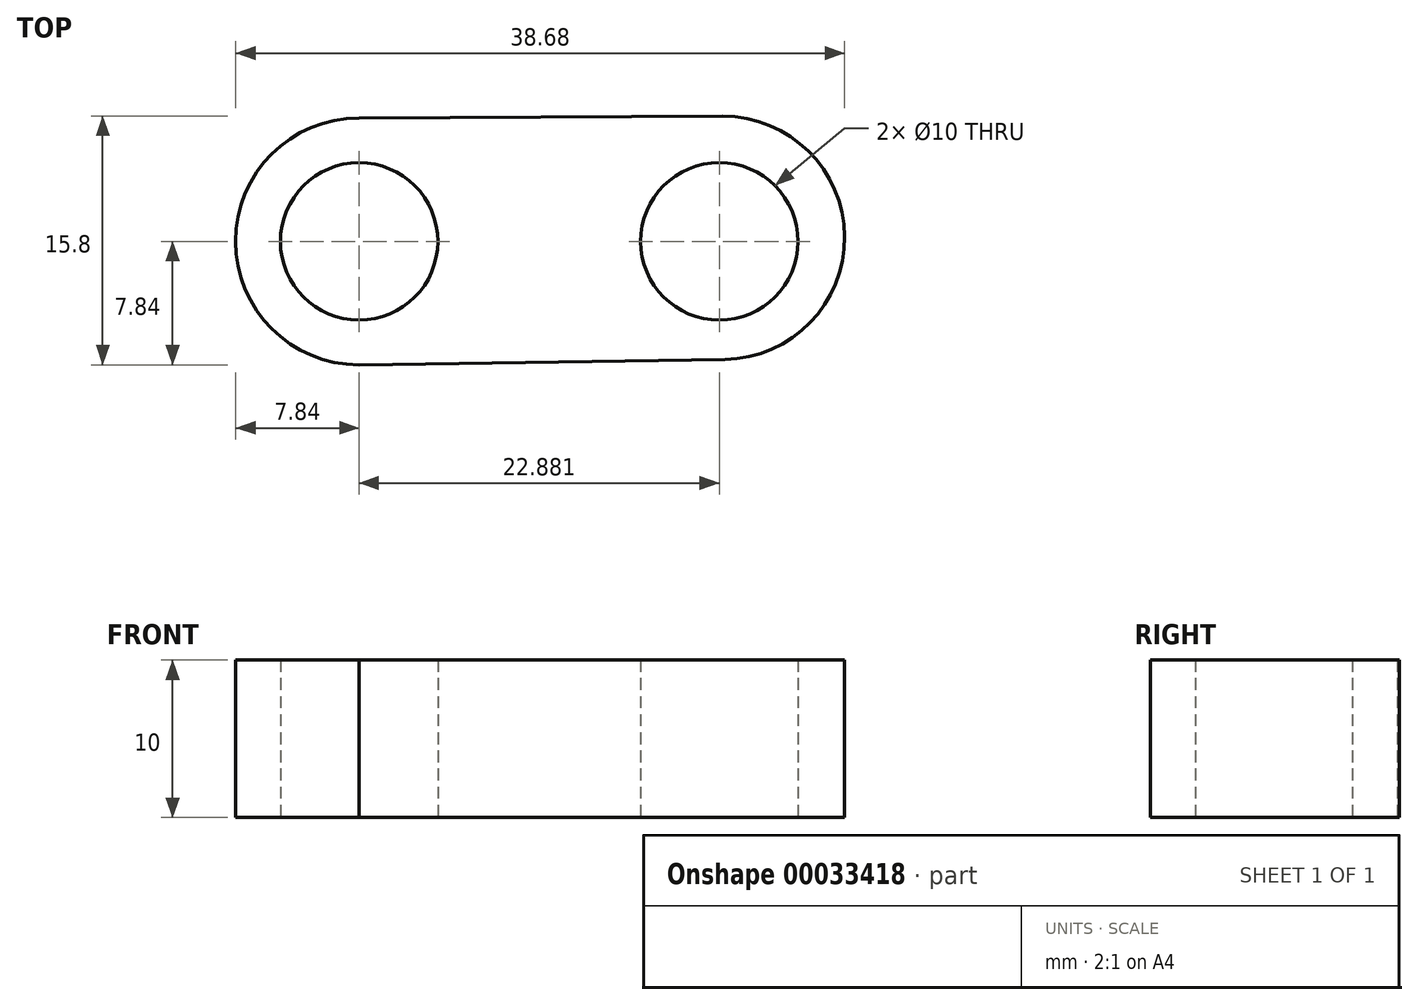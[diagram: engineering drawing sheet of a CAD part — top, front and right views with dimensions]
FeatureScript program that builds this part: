
annotation { "Feature Type Name" : "Feature", "Feature Type Description" : "" }
export const myFeature = defineFeature(function(context is Context, id is Id, definition is map)
    precondition{}
    {
        {
            var Q0;
            Q0=qCreatedBy(makeId("Top.planeOp"),FACE);
            var sketch = newSketch(context, id + "F0", { "sketchPlane" : qUnion([Q0])});
            skCircle(sketch, "E0", {"center": v(0, 0) * mm, "radius": 7.84 * mm});
            skCircle(sketch, "E1", {"center": v(0, 0) * mm, "radius": 5 * mm});
            skCircle(sketch, "E2", {"center": v(22.88, 0) * mm, "radius": 5 * mm});
            skCircle(sketch, "E3", {"center": v(23.11, 0.23) * mm, "radius": 7.72 * mm});
            skLineSegment(sketch, "E4", {"start": v(0, 7.84) * mm, "end": v(23.08, 7.96) * mm});
            skLineSegment(sketch, "E5", {"start": v(0, -7.84) * mm, "end": v(23.23, -7.5) * mm});
            skSolve(sketch);
        }
        {
            var Q0;
            Q0=makeQuery(id+"F0.imprint","IMPRINT",FACE,{"disambiguationData":[TD([[makeQuery(id+"F0.imprint","IMPRINT",EDGE,{"derivedFrom":sQuery(id+"F0.wireOp",EDGE,"E1")}),-1.0]])]});
            var Q1;
            {var subQ5=sQuery(id+"F0.wireOp",EDGE,"E4");Q1=makeQuery(id+"F0.imprint","IMPRINT",FACE,{"disambiguationData":[TD([[makeQuery(id+"F0.imprint","IMPRINT",EDGE,{"derivedFrom":subQ5}),-1.0]])]});}
            var Q2;
            Q2=makeQuery(id+"F0.imprint","IMPRINT",FACE,{"disambiguationData":[TD([[makeQuery(id+"F0.imprint","IMPRINT",EDGE,{"derivedFrom":sQuery(id+"F0.wireOp",EDGE,"E2")}),-1.0]])]});
            extrude(context, id + "F1", {"entities" : qUnion([Q0, Q1, Q2]), "depth" : 10 * mm});
        }
    });
